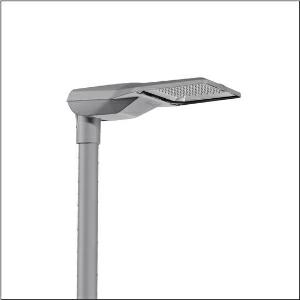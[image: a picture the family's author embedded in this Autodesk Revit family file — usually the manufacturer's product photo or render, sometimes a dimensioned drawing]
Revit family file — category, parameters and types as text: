
# Revit family: streetlight_sl_21_midi___st0_8a_5xe7c43a08lb_78a7
name_source: partatom
category: Lighting Fixtures
units: mm (PartAtom-declared; Revit-internal decimal feet)

## family parameters
Cut with Voids When Loaded = No
Host = Face
Light Source = No
Part Type = Normal
Room Calculation Point = No
Round Connector Dimension = Use Diameter
Shared = No

## types (1)
- --- (1 x LED, 14950 lm, 98.3 W, 4000K)
    Apparent Load = 98 VA
    CIE Flux Codes = 38 75 97 100 100
    Color Rendering = 70
    Color Temperature = 4000K
    Default Elevation = 1800 mm
    Description = Streetlight SL 21 midi, mast luminaire, primary light control with lens, of PMMA, primary optical cover: cover, of toughened safety glass, transparent, light distribution: ST0.8a, light emission: direct distribution, primary light characteristic: asymmetric, installation type: post-top, side-entry, LED, 3G 1.5mm², High Power LED, rated luminous flux: 14.950lm, luminous efficacy: 152lm/W, light colour: 740, colour temperature: 4000K, control: overheat protection, constant luminous flux control, time-dependent luminous flux control, flexible luminous flux parameterisation, mains connection: 220..240V, AC, 50/60Hz, connection cable pre-assembled, cable length: 10,5m, wiring characteristics: H07RN-F, start of lifetime: 98W, end of service life: 101W, reduction: 45W, luminaire housing, of diecast aluminium, powder-coated, Siteco® metallic grey (DB 702S), corrosivity category C5 mid according to DIN EN ISO 12944, please order mast flange separately, inclination adjustable: 0°, 5°, 10°, 15°, sealing non-destructively replaceable, multi-level sealing system, length: 644mm, width: 335mm, height: 110mm, mast flange for spigot size: 42mm (side-entry): 5XC10008XM4, 60/48mm (side-entry/post-top): 5XC10108XM2, 76/60mm (side-entry/post-top): 5XC10108XM1, protection rating (complete): IP66, insulation class (complete): insulation class II (safety insulation), certification: CE, ENEC, ENEC+, VDE, impact resistance: IK09, permissible operating ambient temperature for outdoor applications: -40..+50°C, standard-compliant lighting for roads and squares, packaging unit: 1 piece

Light Distribution: ST0.8a
    Height = 111 mm
    Lamp = 1 x LED
    Lamp Light Flux = 14950 lm
    Lamp Power = 98.3 W
    Lamp count = 1
    Length = 644 mm
    Luminous efficacy = 152 lm/W
    Manufacturer = Siteco
    ModVariant = No
    Model = 5XE7C43A08LB
    Number of Poles = 1
    OnlyDefault = Yes
    Power Factor = 1
    Product Name = Streetlight SL 21 midi | ST0.8a
    Product group = mast luminaire | pylon top
    ProductGroupID = 6100
    Protection Class = Protection class II
    Protection Degree = IP 66
    RLX_Detail_Level = 1
    RLX_Emergency_Light_Flux = 0 lm
    RLX_Emergency_Type = 0
    RLX_Emergency_Type_DB = No
    RlxData = <blob elided: 90889 chars, md5=73356676>
    Socket = socket
    Standby Power = 0 W
    System Light Flux = 14950 lm
    System Power = 98 W
    Type Comments = factory setting: luminous flux: 100 % | Output Level: 100 % | 1020 mA
    Type Image = l_1004298.jpg
    URL = http://relux.com
    VarID = @adj_137473
    Voltage = 0 V
    Weight = 0.00 kg
    Width = 336 mm

## geometry (parser evidence)
native form markers: Blend x4, Sweep x11
no freeform markers — native parametric forms only
